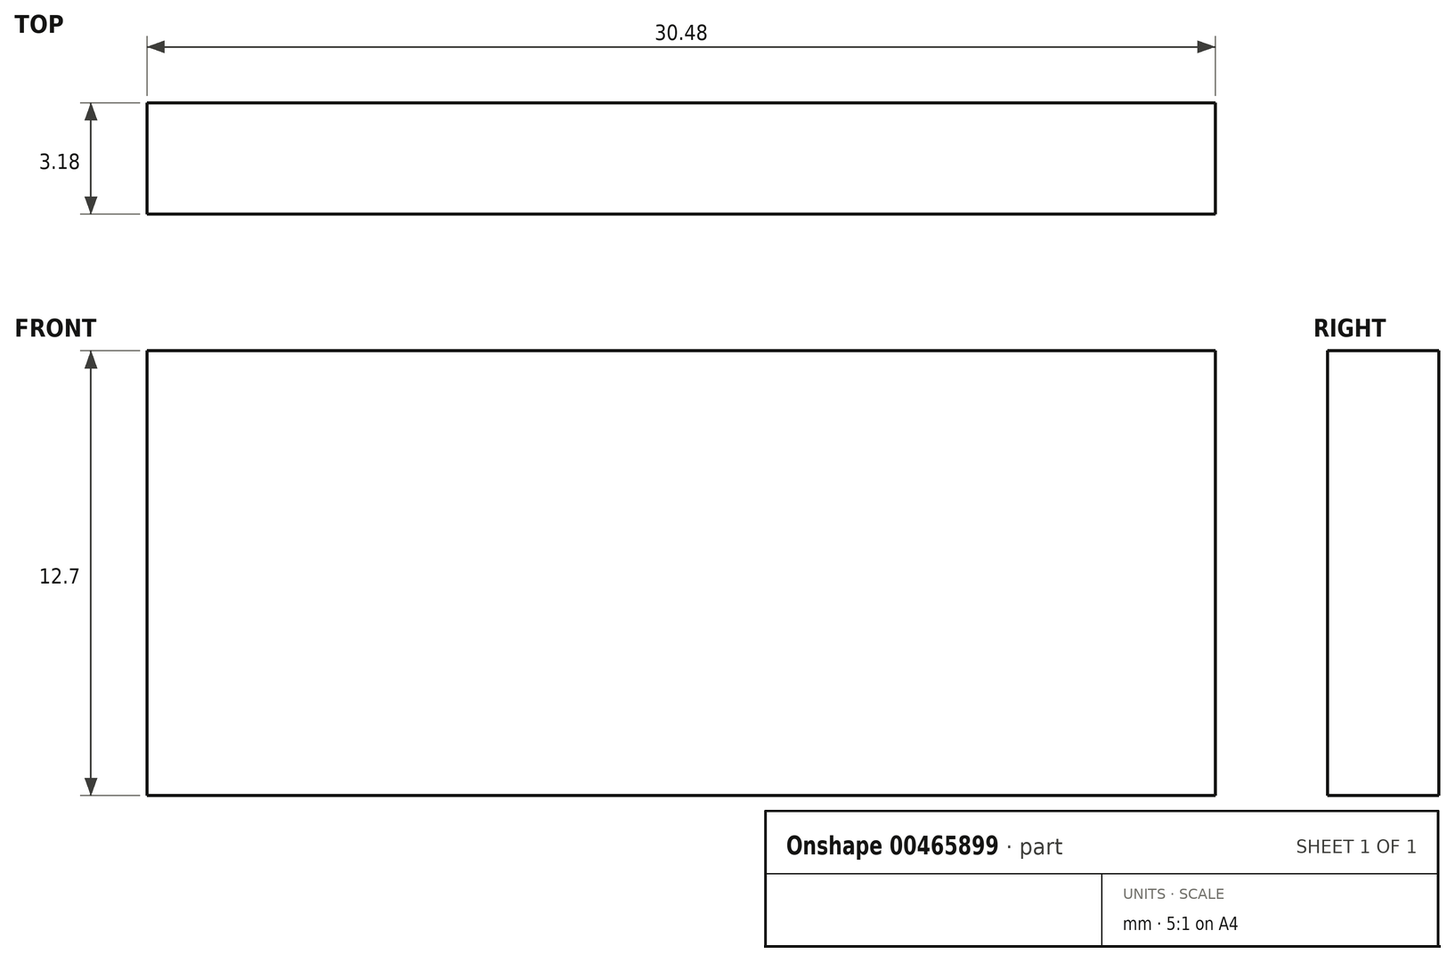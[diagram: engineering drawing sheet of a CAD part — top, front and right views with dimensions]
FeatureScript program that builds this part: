
annotation { "Feature Type Name" : "Feature", "Feature Type Description" : "" }
export const myFeature = defineFeature(function(context is Context, id is Id, definition is map)
    precondition{}
    {
        {
            var Q0;
            Q0=qCreatedBy(makeId("Front.planeOp"),FACE);
            var sketch = newSketch(context, id + "F0", { "sketchPlane" : qUnion([Q0])});
            skLineSegment(sketch, "E0.bottom", {"start": v(-15.24, 6.35) * mm, "end": v(15.24, 6.35) * mm});
            skLineSegment(sketch, "E0.top", {"start": v(-15.24, -6.35) * mm, "end": v(15.24, -6.35) * mm});
            skLineSegment(sketch, "E0.left", {"start": v(-15.24, 6.35) * mm, "end": v(-15.24, -6.35) * mm});
            skLineSegment(sketch, "E0.right", {"start": v(15.24, 6.35) * mm, "end": v(15.24, -6.35) * mm});
            skPoint(sketch, "E0.middle", {"position": v(0, 0) * mm});
            skSolve(sketch);
        }
        {
            var Q0;
            Q0=makeQuery(id+"F0.imprint","IMPRINT",FACE,{"disambiguationData":[TD([[makeQuery(id+"F0.imprint","IMPRINT",EDGE,{"derivedFrom":sQuery(id+"F0.wireOp",EDGE,"E0.bottom")}),-1.0]])]});
            extrude(context, id + "F1", {"entities" : qUnion([Q0]), "endBound" : BoundingType.SYMMETRIC, "depth" : 3.17 * mm});
        }
    });
